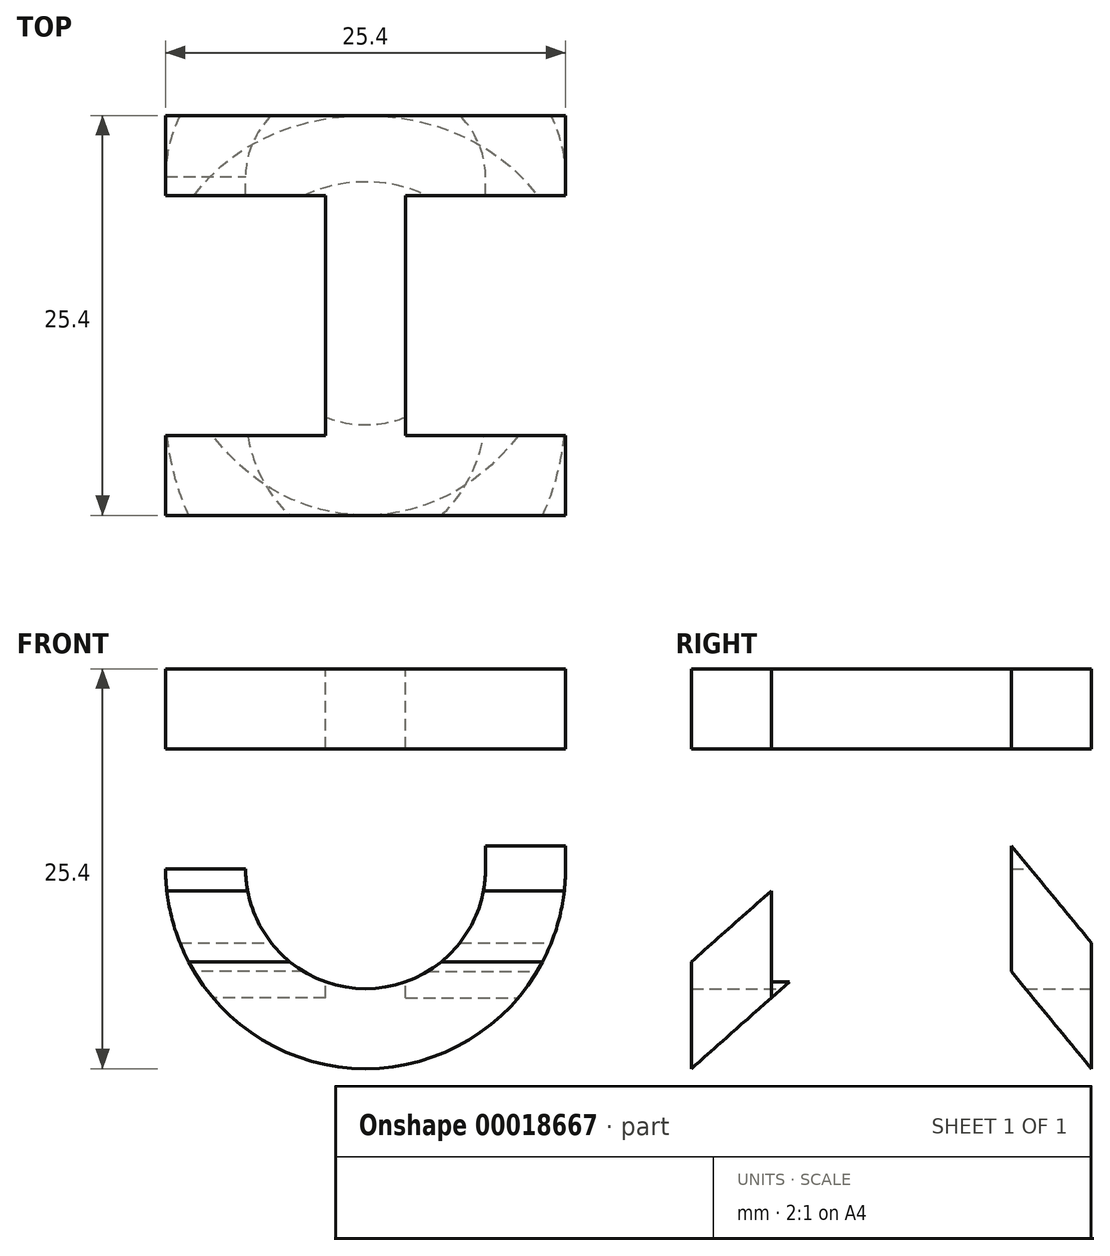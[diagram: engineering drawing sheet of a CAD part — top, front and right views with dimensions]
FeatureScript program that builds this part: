
annotation { "Feature Type Name" : "Feature", "Feature Type Description" : "" }
export const myFeature = defineFeature(function(context is Context, id is Id, definition is map)
    precondition{}
    {
        {
            var Q0;
            Q0=qCreatedBy(makeId("Front.planeOp"),FACE);
            var sketch = newSketch(context, id + "F0", { "sketchPlane" : qUnion([Q0])});
            skLineSegment(sketch, "E0", {"start": v(0, 0) * mm, "end": v(-25.4, 0) * mm});
            skLineSegment(sketch, "E1", {"start": v(-25.4, 0) * mm, "end": v(-25.4, -5.08) * mm});
            skLineSegment(sketch, "E2", {"start": v(-25.4, -5.08) * mm, "end": v(-5.08, -5.08) * mm});
            skLineSegment(sketch, "E3", {"start": v(-5.08, -5.08) * mm, "end": v(-5.08, -12.7) * mm});
            skArc(sketch, "E4", {"start": v(-20.32, -12.7) * mm, "mid": v(-12.7, -20.32) * mm, "end": v(-5.08, -12.7) * mm});
            skLineSegment(sketch, "E5", {"start": v(-20.32, -12.7) * mm, "end": v(-25.4, -12.7) * mm});
            skArc(sketch, "E6", {"start": v(-25.4, -12.7) * mm, "mid": v(-12.7, -25.4) * mm, "end": v(0, -12.7) * mm});
            skLineSegment(sketch, "E7", {"start": v(0, -12.7) * mm, "end": v(0, 0) * mm});
            skSolve(sketch);
        }
        {
            var Q0;
            Q0 = qSketchRegion(id + "F0", true);
            extrude(context, id + "F1", {"entities" : qUnion([Q0]), "depth" : 25.4 * mm});
        }
        {
            var Q0;
            Q0=makeQuery(id+"F1.opExtrude","SWEPT_FACE",FACE,{"disambiguationData":[OSD([sQuery(id+"F0.wireOp",EDGE,"E7")])]});
            var sketch = newSketch(context, id + "F2", { "sketchPlane" : qUnion([Q0])});
            skLineSegment(sketch, "E8", {"start": v(-25.4, -5.08) * mm, "end": v(-16.74, -5.08) * mm});
            skLineSegment(sketch, "E9", {"start": v(-16.74, -5.08) * mm, "end": v(-13.96, -8.45) * mm});
            skLineSegment(sketch, "E10", {"start": v(-13.96, -8.45) * mm, "end": v(-25.4, -18.6) * mm});
            skLineSegment(sketch, "E11", {"start": v(-25.4, -18.6) * mm, "end": v(-25.4, -5.08) * mm});
            skLineSegment(sketch, "E12.0", {"start": v(-25.4, -25.4) * mm, "end": v(-25.4, -12.7) * mm});
            skLineSegment(sketch, "E13", {"start": v(-25.4, -25.4) * mm, "end": v(-10.73, -12.38) * mm});
            skLineSegment(sketch, "E14", {"start": v(-10.73, -12.38) * mm, "end": v(0, -25.4) * mm});
            skLineSegment(sketch, "E15", {"start": v(0, -25.4) * mm, "end": v(-25.4, -25.4) * mm});
            skLineSegment(sketch, "E16", {"start": v(0, -17.41) * mm, "end": v(-10.16, -5.08) * mm});
            skLineSegment(sketch, "E17", {"start": v(-10.16, -5.08) * mm, "end": v(0, -5.08) * mm});
            skLineSegment(sketch, "E18", {"start": v(0, -5.08) * mm, "end": v(0, -17.41) * mm});
            skLineSegment(sketch, "E19", {"start": v(-3.88, -12.7) * mm, "end": v(-7.8, -15.93) * mm, "construction": true});
            skSolve(sketch);
        }
        {
            var Q0;
            Q0 = qSketchRegion(id + "F2", true);
            extrude(context, id + "F3", {"entities" : qUnion([Q0]), "operationType" : NewBodyOperationType.REMOVE, "endBound" : BoundingType.THROUGH_ALL, "oppositeDirection" : true, "depth" : 25.4 * mm});
        }
        {
            var Q0;
            Q0=makeQuery(id+"F1.opExtrude","SWEPT_FACE",FACE,{"disambiguationData":[OSD([sQuery(id+"F0.wireOp",EDGE,"E0")])]});
            var sketch = newSketch(context, id + "F4", { "sketchPlane" : qUnion([Q0])});
            skLineSegment(sketch, "E20.bottom", {"start": v(-25.4, -5.08) * mm, "end": v(-15.24, -5.08) * mm});
            skLineSegment(sketch, "E20.top", {"start": v(-25.4, -20.32) * mm, "end": v(-15.24, -20.32) * mm});
            skLineSegment(sketch, "E20.left", {"start": v(-25.4, -5.08) * mm, "end": v(-25.4, -20.32) * mm});
            skLineSegment(sketch, "E20.right", {"start": v(-15.24, -5.08) * mm, "end": v(-15.24, -20.32) * mm});
            skLineSegment(sketch, "E21.bottom", {"start": v(0, -5.08) * mm, "end": v(-10.16, -5.08) * mm});
            skLineSegment(sketch, "E21.top", {"start": v(0, -20.32) * mm, "end": v(-10.16, -20.32) * mm});
            skLineSegment(sketch, "E21.left", {"start": v(0, -5.08) * mm, "end": v(0, -20.32) * mm});
            skLineSegment(sketch, "E21.right", {"start": v(-10.16, -5.08) * mm, "end": v(-10.16, -20.32) * mm});
            skSolve(sketch);
        }
        {
            var Q0;
            Q0 = qSketchRegion(id + "F4", true);
            extrude(context, id + "F5", {"entities" : qUnion([Q0]), "operationType" : NewBodyOperationType.REMOVE, "oppositeDirection" : true, "depth" : 25.4 * mm});
        }
    });
